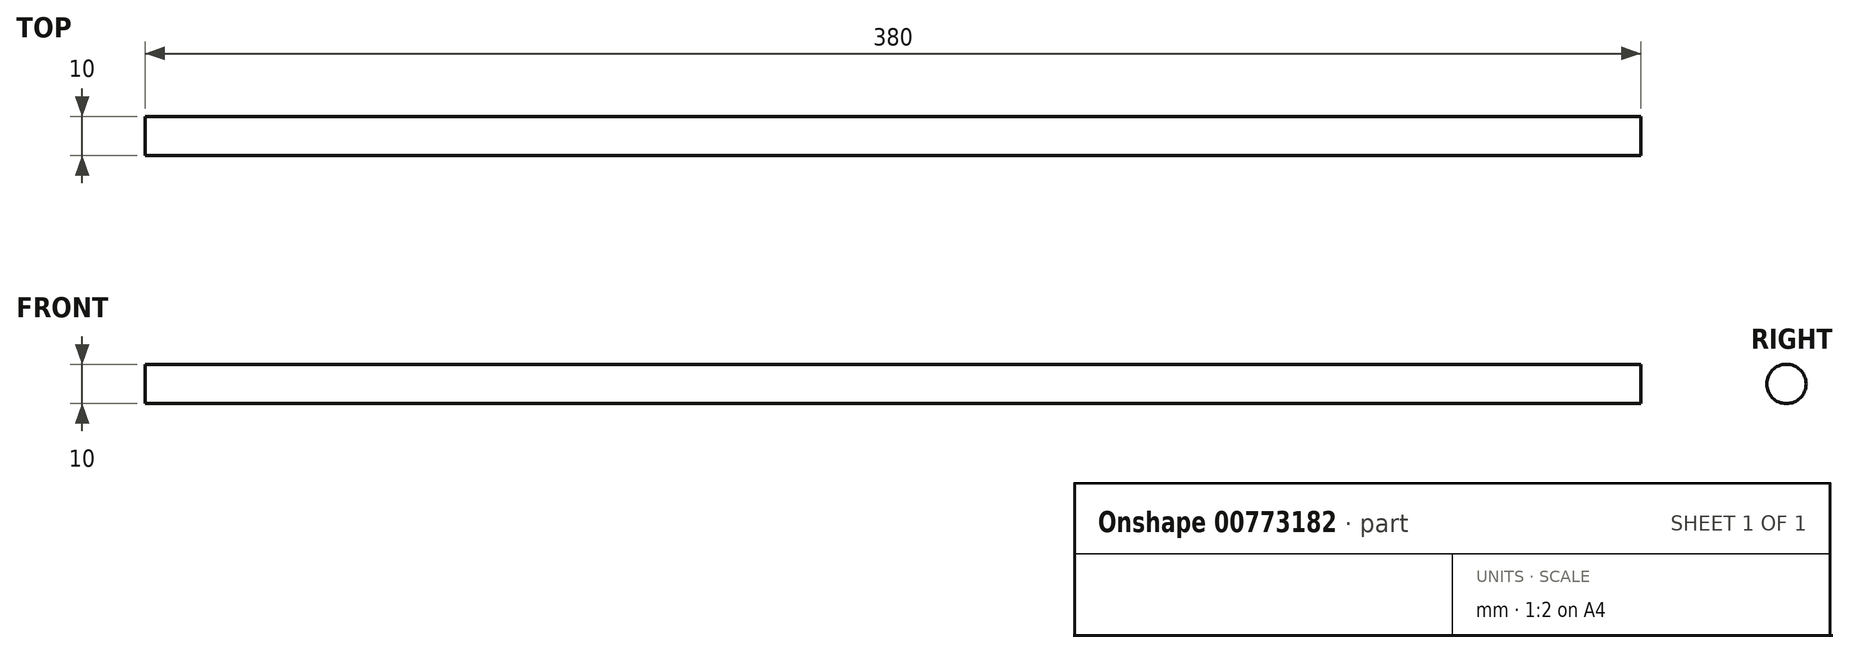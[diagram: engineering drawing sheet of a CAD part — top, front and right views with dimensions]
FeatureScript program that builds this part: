
annotation { "Feature Type Name" : "Feature", "Feature Type Description" : "" }
export const myFeature = defineFeature(function(context is Context, id is Id, definition is map)
    precondition{}
    {
        {
            var Q0;
            Q0=qCreatedBy(makeId("Right.planeOp"),FACE);
            var sketch = newSketch(context, id + "F0", { "sketchPlane" : qUnion([Q0])});
            skCircle(sketch, "E0", {"center": v(0, 0) * mm, "radius": 5 * mm});
            skSolve(sketch);
        }
        {
            var Q0;
            Q0 = qSketchRegion(id + "F0", true);
            extrude(context, id + "F1", {"entities" : qUnion([Q0]), "depth" : 380 * mm, "offsetDistance" : 25 * mm});
        }
    });
